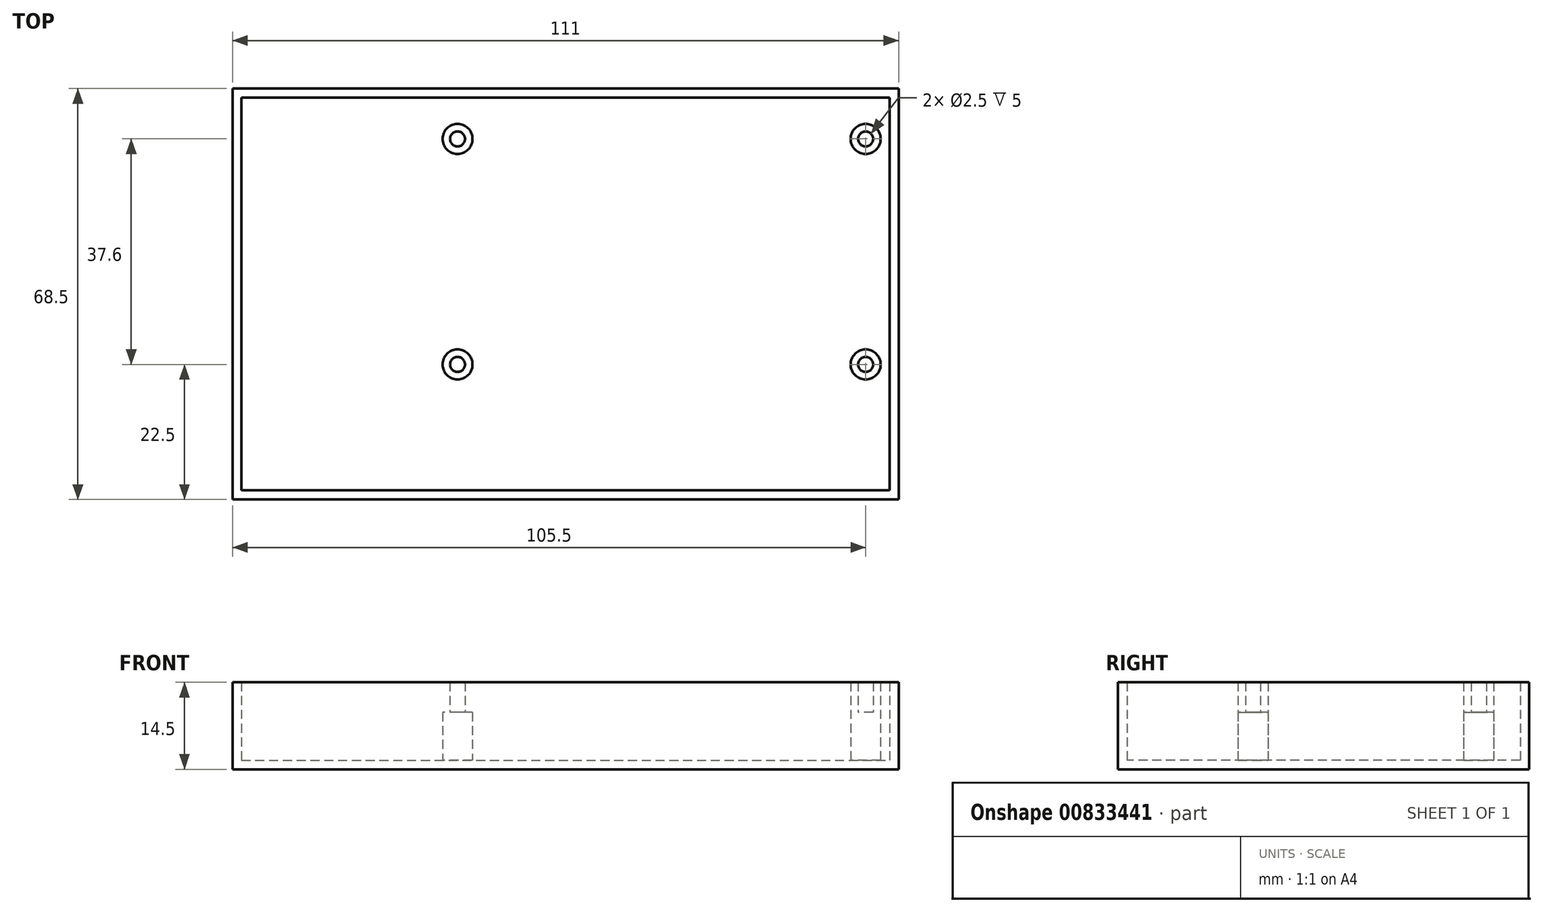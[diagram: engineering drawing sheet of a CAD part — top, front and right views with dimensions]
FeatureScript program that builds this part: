
annotation { "Feature Type Name" : "Feature", "Feature Type Description" : "" }
export const myFeature = defineFeature(function(context is Context, id is Id, definition is map)
    precondition{}
    {
        {
            var Q0;
            Q0=qCreatedBy(makeId("Top.planeOp"),FACE);
            var sketch = newSketch(context, id + "F0", { "sketchPlane" : qUnion([Q0])});
            skLineSegment(sketch, "E0.bottom", {"start": v(-36.5, 30) * mm, "end": v(36.5, 30) * mm, "construction": true});
            skLineSegment(sketch, "E0.top", {"start": v(-36.5, -30) * mm, "end": v(36.5, -30) * mm, "construction": true});
            skLineSegment(sketch, "E0.left", {"start": v(-36.5, 30) * mm, "end": v(-36.5, -30) * mm, "construction": true});
            skLineSegment(sketch, "E0.right", {"start": v(36.5, 30) * mm, "end": v(36.5, -30) * mm, "construction": true});
            skPoint(sketch, "E0.middle", {"position": v(0, 0) * mm});
            skCircle(sketch, "E1", {"center": v(-34, 27.1) * mm, "radius": 1.25 * mm});
            skCircle(sketch, "E2", {"center": v(-34, -10.5) * mm, "radius": 1.25 * mm});
            skCircle(sketch, "E3.MirrorC", {"center": v(34, 27.1) * mm, "radius": 1.25 * mm});
            skCircle(sketch, "E4.MirrorC", {"center": v(34, -10.5) * mm, "radius": 1.25 * mm});
            skLineSegment(sketch, "E5.bottom", {"start": v(-70, 34) * mm, "end": v(38, 34) * mm});
            skLineSegment(sketch, "E5.top", {"start": v(-70, -31.5) * mm, "end": v(38, -31.5) * mm});
            skLineSegment(sketch, "E5.left", {"start": v(-70, 34) * mm, "end": v(-70, -31.5) * mm});
            skLineSegment(sketch, "E5.right", {"start": v(38, 34) * mm, "end": v(38, -31.5) * mm});
            skCircle(sketch, "E6", {"center": v(-34, 27.1) * mm, "radius": 2.5 * mm});
            skCircle(sketch, "E7", {"center": v(-34, -10.5) * mm, "radius": 2.5 * mm});
            skCircle(sketch, "E8", {"center": v(34, -10.5) * mm, "radius": 2.5 * mm});
            skCircle(sketch, "E9", {"center": v(34, 27.1) * mm, "radius": 2.5 * mm});
            skLineSegment(sketch, "E10.bottom", {"start": v(-68.5, 30) * mm, "end": v(-38.5, 30) * mm, "construction": true});
            skLineSegment(sketch, "E10.top", {"start": v(-68.5, -24) * mm, "end": v(-38.5, -24) * mm, "construction": true});
            skLineSegment(sketch, "E10.left", {"start": v(-68.5, 30) * mm, "end": v(-68.5, -24) * mm, "construction": true});
            skLineSegment(sketch, "E10.right", {"start": v(-38.5, 30) * mm, "end": v(-38.5, -24) * mm, "construction": true});
            skLineSegment(sketch, "E11.0", {"start": v(-71.5, 35.5) * mm, "end": v(39.5, 35.5) * mm});
            skLineSegment(sketch, "E11.1", {"start": v(-71.5, 35.5) * mm, "end": v(-71.5, -33) * mm});
            skLineSegment(sketch, "E11.2", {"start": v(-71.5, -33) * mm, "end": v(39.5, -33) * mm});
            skLineSegment(sketch, "E11.3", {"start": v(39.5, 35.5) * mm, "end": v(39.5, -33) * mm});
            skSolve(sketch);
        }
        {
            var Q0;
            Q0 = qSketchRegion(id + "F0", true);
            var Q1;
            Q1=makeQuery(id+"F0.imprint","IMPRINT",FACE,{"disambiguationData":[TD([[makeQuery(id+"F0.imprint","IMPRINT",EDGE,{"derivedFrom":sQuery(id+"F0.wireOp",EDGE,"E5.bottom")}),-1.0]])]});
            var Q2;
            Q2=makeQuery(id+"F0.imprint","IMPRINT",FACE,{"disambiguationData":[TD([[makeQuery(id+"F0.imprint","IMPRINT",EDGE,{"derivedFrom":sQuery(id+"F0.wireOp",EDGE,"E2")}),-1.0]])]});
            var Q3;
            Q3=makeQuery(id+"F0.imprint","IMPRINT",FACE,{"disambiguationData":[TD([[makeQuery(id+"F0.imprint","IMPRINT",EDGE,{"derivedFrom":sQuery(id+"F0.wireOp",EDGE,"E2")}),1.0]])]});
            var Q4;
            Q4=makeQuery(id+"F0.imprint","IMPRINT",FACE,{"disambiguationData":[TD([[makeQuery(id+"F0.imprint","IMPRINT",EDGE,{"derivedFrom":sQuery(id+"F0.wireOp",EDGE,"E4.MirrorC")}),1.0]])]});
            var Q5;
            Q5=makeQuery(id+"F0.imprint","IMPRINT",FACE,{"disambiguationData":[TD([[makeQuery(id+"F0.imprint","IMPRINT",EDGE,{"derivedFrom":sQuery(id+"F0.wireOp",EDGE,"E4.MirrorC")}),-1.0]])]});
            var Q6;
            Q6=makeQuery(id+"F0.imprint","IMPRINT",FACE,{"disambiguationData":[TD([[makeQuery(id+"F0.imprint","IMPRINT",EDGE,{"derivedFrom":sQuery(id+"F0.wireOp",EDGE,"E3.MirrorC")}),1.0]])]});
            var Q7;
            Q7=makeQuery(id+"F0.imprint","IMPRINT",FACE,{"disambiguationData":[TD([[makeQuery(id+"F0.imprint","IMPRINT",EDGE,{"derivedFrom":sQuery(id+"F0.wireOp",EDGE,"E3.MirrorC")}),-1.0]])]});
            var Q8;
            Q8=makeQuery(id+"F0.imprint","IMPRINT",FACE,{"disambiguationData":[TD([[makeQuery(id+"F0.imprint","IMPRINT",EDGE,{"derivedFrom":sQuery(id+"F0.wireOp",EDGE,"E1")}),-1.0]])]});
            var Q9;
            Q9=makeQuery(id+"F0.imprint","IMPRINT",FACE,{"disambiguationData":[TD([[makeQuery(id+"F0.imprint","IMPRINT",EDGE,{"derivedFrom":sQuery(id+"F0.wireOp",EDGE,"E1")}),1.0]])]});
            extrude(context, id + "F1", {"entities" : qUnion([Q0, Q1, Q2, Q3, Q4, Q5, Q6, Q7, Q8, Q9]), "oppositeDirection" : true, "depth" : 1.5 * mm, "offsetDistance" : 25 * mm});
        }
        {
            var Q0;
            Q0=makeQuery(id+"F0.imprint","IMPRINT",FACE,{"disambiguationData":[TD([[makeQuery(id+"F0.imprint","IMPRINT",EDGE,{"derivedFrom":sQuery(id+"F0.wireOp",EDGE,"E5.bottom")}),1.0]])]});
            var Q1;
            Q1=makeQuery(id+"F0.imprint","IMPRINT",FACE,{"disambiguationData":[TD([[makeQuery(id+"F0.imprint","IMPRINT",EDGE,{"derivedFrom":sQuery(id+"F0.wireOp",EDGE,"E1")}),1.0]])]});
            var Q2;
            Q2=makeQuery(id+"F0.imprint","IMPRINT",FACE,{"disambiguationData":[TD([[makeQuery(id+"F0.imprint","IMPRINT",EDGE,{"derivedFrom":sQuery(id+"F0.wireOp",EDGE,"E3.MirrorC")}),-1.0]])]});
            var Q3;
            Q3=makeQuery(id+"F0.imprint","IMPRINT",FACE,{"disambiguationData":[TD([[makeQuery(id+"F0.imprint","IMPRINT",EDGE,{"derivedFrom":sQuery(id+"F0.wireOp",EDGE,"E4.MirrorC")}),-1.0]])]});
            var Q4;
            Q4=makeQuery(id+"F0.imprint","IMPRINT",FACE,{"disambiguationData":[TD([[makeQuery(id+"F0.imprint","IMPRINT",EDGE,{"derivedFrom":sQuery(id+"F0.wireOp",EDGE,"E2")}),1.0]])]});
            extrude(context, id + "F2", {"entities" : qUnion([Q0, Q1, Q2, Q3, Q4]), "operationType" : NewBodyOperationType.ADD, "depth" : (22 - 9) * mm, "offsetDistance" : 25 * mm});
        }
        {
            var Q0;
            Q0=makeQuery(id+"F0.imprint","IMPRINT",FACE,{"disambiguationData":[TD([[makeQuery(id+"F0.imprint","IMPRINT",EDGE,{"derivedFrom":sQuery(id+"F0.wireOp",EDGE,"E1")}),-1.0]])]});
            var Q1;
            Q1=makeQuery(id+"F0.imprint","IMPRINT",FACE,{"disambiguationData":[TD([[makeQuery(id+"F0.imprint","IMPRINT",EDGE,{"derivedFrom":sQuery(id+"F0.wireOp",EDGE,"E2")}),-1.0]])]});
            var Q2;
            Q2=makeQuery(id+"F0.imprint","IMPRINT",FACE,{"disambiguationData":[TD([[makeQuery(id+"F0.imprint","IMPRINT",EDGE,{"derivedFrom":sQuery(id+"F0.wireOp",EDGE,"E3.MirrorC")}),1.0]])]});
            var Q3;
            Q3=makeQuery(id+"F0.imprint","IMPRINT",FACE,{"disambiguationData":[TD([[makeQuery(id+"F0.imprint","IMPRINT",EDGE,{"derivedFrom":sQuery(id+"F0.wireOp",EDGE,"E4.MirrorC")}),1.0]])]});
            extrude(context, id + "F3", {"entities" : qUnion([Q0, Q1, Q2, Q3]), "operationType" : NewBodyOperationType.ADD, "depth" : (22 - 14) * mm, "offsetDistance" : 25 * mm});
        }
    });
